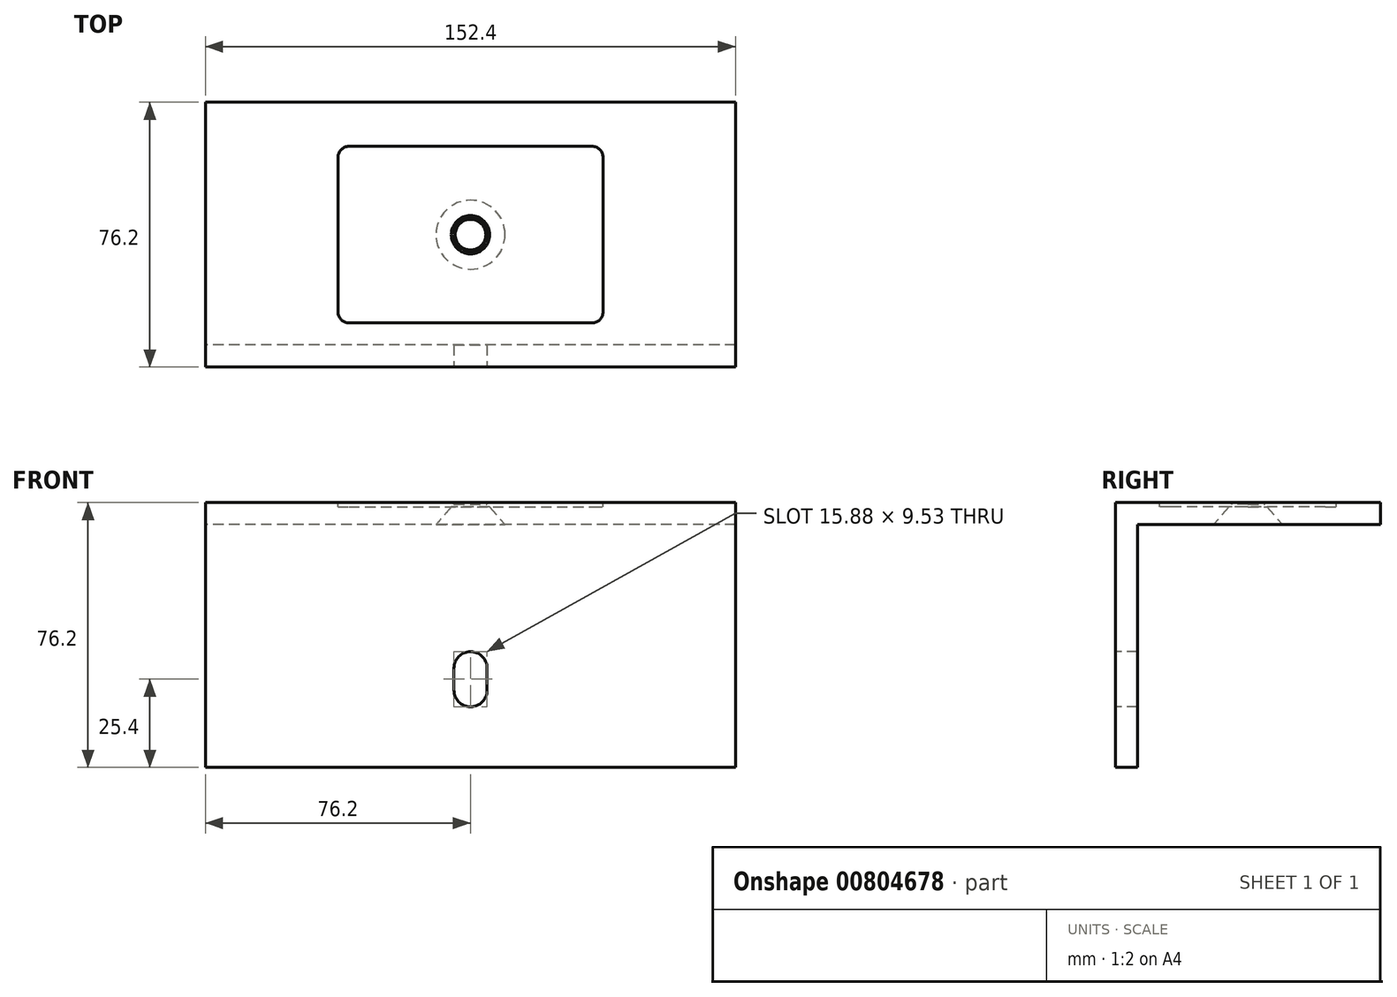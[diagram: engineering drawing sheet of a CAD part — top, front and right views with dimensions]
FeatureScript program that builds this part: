
annotation { "Feature Type Name" : "Feature", "Feature Type Description" : "" }
export const myFeature = defineFeature(function(context is Context, id is Id, definition is map)
    precondition{}
    {
        {
            var Q0;
            Q0=qCreatedBy(makeId("Right.planeOp"),FACE);
            var sketch = newSketch(context, id + "F0", { "sketchPlane" : qUnion([Q0])});
            skLineSegment(sketch, "E0", {"start": v(76.2, 0) * mm, "end": v(0, 0) * mm});
            skLineSegment(sketch, "E1", {"start": v(0, 0) * mm, "end": v(0, -76.2) * mm});
            skLineSegment(sketch, "E2", {"start": v(0, -76.2) * mm, "end": v(6.35, -76.2) * mm});
            skLineSegment(sketch, "E3", {"start": v(6.35, -76.2) * mm, "end": v(6.35, -6.35) * mm});
            skLineSegment(sketch, "E4", {"start": v(6.35, -6.35) * mm, "end": v(76.2, -6.35) * mm});
            skLineSegment(sketch, "E5", {"start": v(76.2, -6.35) * mm, "end": v(76.2, 0) * mm});
            skSolve(sketch);
        }
        {
            var Q0;
            Q0=makeQuery(id+"F0.imprint","IMPRINT",FACE,{"disambiguationData":[TD([[makeQuery(id+"F0.imprint","IMPRINT",EDGE,{"derivedFrom":sQuery(id+"F0.wireOp",EDGE,"E0")}),1.0]])]});
            extrude(context, id + "F1", {"entities" : qUnion([Q0]), "depth" : 152.4 * mm, "offsetDistance" : 25.4 * mm});
        }
        {
            var Q0;
            Q0=makeQuery(id+"F1.opExtrude","SWEPT_FACE",FACE,{"disambiguationData":[OSD([sQuery(id+"F0.wireOp",EDGE,"E4")])]});
            var sketch = newSketch(context, id + "F2", { "sketchPlane" : qUnion([Q0])});
            skPoint(sketch, "E6", {"position": v(76.2, -38.1) * mm});
            skSolve(sketch);
        }
        {
            var Q0;
            Q0=sQuery(id+"F2.wireOp",VERTEX,"4effdeb6-b71b-466a-b377-efdbb7cfd678");
            var Q1;
            Q1=sQuery(id+"F2.wireOp",VERTEX,"E6");
            var Q2;
            Q2=makeQuery(id+"F1.opExtrude","SWEPT_BODY",BODY,{"disambiguationData":[OSD([sQuery(id+"F0.wireOp",EDGE,"E0"),sQuery(id+"F0.wireOp",EDGE,"E1"),sQuery(id+"F0.wireOp",EDGE,"E2"),sQuery(id+"F0.wireOp",EDGE,"E3"),sQuery(id+"F0.wireOp",EDGE,"E4"),sQuery(id+"F0.wireOp",EDGE,"E5")])]});
            hole(context, id + "F3", {"style" : HoleStyle.C_SINK, "endStyle" : HoleEndStyle.THROUGH, "standardTappedOrClearance" : lookupTablePath({ "standard" : "ANSI", "size" : "3/8 (0.38)", "type" : "Drilled" }), "standardBlindInLast" : lookupTablePath({ "standard" : "ANSI", "size" : "3/8", "type" : "Drilled" }), "holeDiameter" : 3 / 203.2 * mm, "cSinkDiameter" : 19.86 * mm, "cSinkAngle" : 82 * degree, "majorDiameter" : 6.35 * mm, "isTappedThrough" : true, "tappedDepth" : 12.7 * mm, "tapClearance" : 3, "locations" : qUnion([Q0, Q1]), "scope" : qUnion([Q2])});
        }
        {
            var Q0;
            Q0=makeQuery(id+"F1.opExtrude","SWEPT_FACE",FACE,{"disambiguationData":[OSD([sQuery(id+"F0.wireOp",EDGE,"E0")])]});
            var sketch = newSketch(context, id + "F4", { "sketchPlane" : qUnion([Q0])});
            skLineSegment(sketch, "E7.bottom", {"start": v(41.27, 63.5) * mm, "end": v(111.13, 63.5) * mm});
            skLineSegment(sketch, "E7.top", {"start": v(41.27, 12.7) * mm, "end": v(111.13, 12.7) * mm});
            skLineSegment(sketch, "E7.left", {"start": v(38.1, 60.32) * mm, "end": v(38.1, 15.87) * mm});
            skLineSegment(sketch, "E7.right", {"start": v(114.3, 60.32) * mm, "end": v(114.3, 15.87) * mm});
            skCircle(sketch, "E8.0", {"center": v(76.2, 38.1) * mm, "radius": 4.76 * mm});
            skLineSegment(sketch, "E9.0.0", {"start": v(0, 76.2) * mm, "end": v(0, 0) * mm});
            skLineSegment(sketch, "E9.0.1", {"start": v(0, 0) * mm, "end": v(152.4, 0) * mm});
            skLineSegment(sketch, "E9.0.2", {"start": v(152.4, 0) * mm, "end": v(152.4, 76.2) * mm});
            skLineSegment(sketch, "E9.0.3", {"start": v(152.4, 76.2) * mm, "end": v(0, 76.2) * mm});
            skPoint(sketch, "E10.visualSharp", {"position": v(38.1, 63.5) * mm});
            skArc(sketch, "E10.filletArc", {"start": v(41.27, 63.5) * mm, "mid": v(39.03, 62.57) * mm, "end": v(38.1, 60.32) * mm});
            skPoint(sketch, "E11.visualSharp", {"position": v(38.1, 12.7) * mm});
            skArc(sketch, "E11.filletArc", {"start": v(38.1, 15.87) * mm, "mid": v(39.03, 13.63) * mm, "end": v(41.27, 12.7) * mm});
            skPoint(sketch, "E12.visualSharp", {"position": v(114.3, 12.7) * mm});
            skArc(sketch, "E12.filletArc", {"start": v(111.13, 12.7) * mm, "mid": v(113.37, 13.63) * mm, "end": v(114.3, 15.87) * mm});
            skPoint(sketch, "E13.visualSharp", {"position": v(114.3, 63.5) * mm});
            skArc(sketch, "E13.filletArc", {"start": v(114.3, 60.32) * mm, "mid": v(113.37, 62.57) * mm, "end": v(111.13, 63.5) * mm});
            skSolve(sketch);
        }
        {
            var Q0;
            Q0=makeQuery(id+"F4.imprint","IMPRINT",FACE,{"disambiguationData":[TD([[makeQuery(id+"F4.imprint","IMPRINT",EDGE,{"derivedFrom":sQuery(id+"F4.wireOp",EDGE,"E7.bottom")}),-1.0]])]});
            extrude(context, id + "F5", {"entities" : qUnion([Q0]), "operationType" : NewBodyOperationType.REMOVE, "oppositeDirection" : true, "depth" : 1.27 * mm, "offsetDistance" : 25.4 * mm});
        }
        {
            var Q0;
            Q0=makeQuery(id+"F1.opExtrude","SWEPT_FACE",FACE,{"disambiguationData":[OSD([sQuery(id+"F0.wireOp",EDGE,"E1")])]});
            var sketch = newSketch(context, id + "F6", { "sketchPlane" : qUnion([Q0])});
            skPoint(sketch, "E14", {"position": v(76.2, -50.8) * mm});
            skPoint(sketch, "E14.positionSnap0", {"position": v(76.2, -76.2) * mm});
            skArc(sketch, "E15", {"start": v(71.44, -53.97) * mm, "mid": v(76.2, -58.74) * mm, "end": v(80.96, -53.97) * mm});
            skArc(sketch, "E16", {"start": v(80.96, -47.62) * mm, "mid": v(76.2, -42.86) * mm, "end": v(71.44, -47.62) * mm});
            skLineSegment(sketch, "E17", {"start": v(71.44, -53.97) * mm, "end": v(71.44, -47.62) * mm});
            skLineSegment(sketch, "E18", {"start": v(80.96, -47.62) * mm, "end": v(80.96, -53.97) * mm});
            skSolve(sketch);
        }
        {
            var Q0;
            Q0=makeQuery(id+"F6.imprint","IMPRINT",FACE,{"disambiguationData":[TD([[makeQuery(id+"F6.imprint","IMPRINT",EDGE,{"derivedFrom":sQuery(id+"F6.wireOp",EDGE,"E15")}),1.0]])]});
            extrude(context, id + "F7", {"entities" : qUnion([Q0]), "operationType" : NewBodyOperationType.REMOVE, "endBound" : BoundingType.THROUGH_ALL, "oppositeDirection" : true, "depth" : 25.4 * mm, "offsetDistance" : 25.4 * mm});
        }
    });
